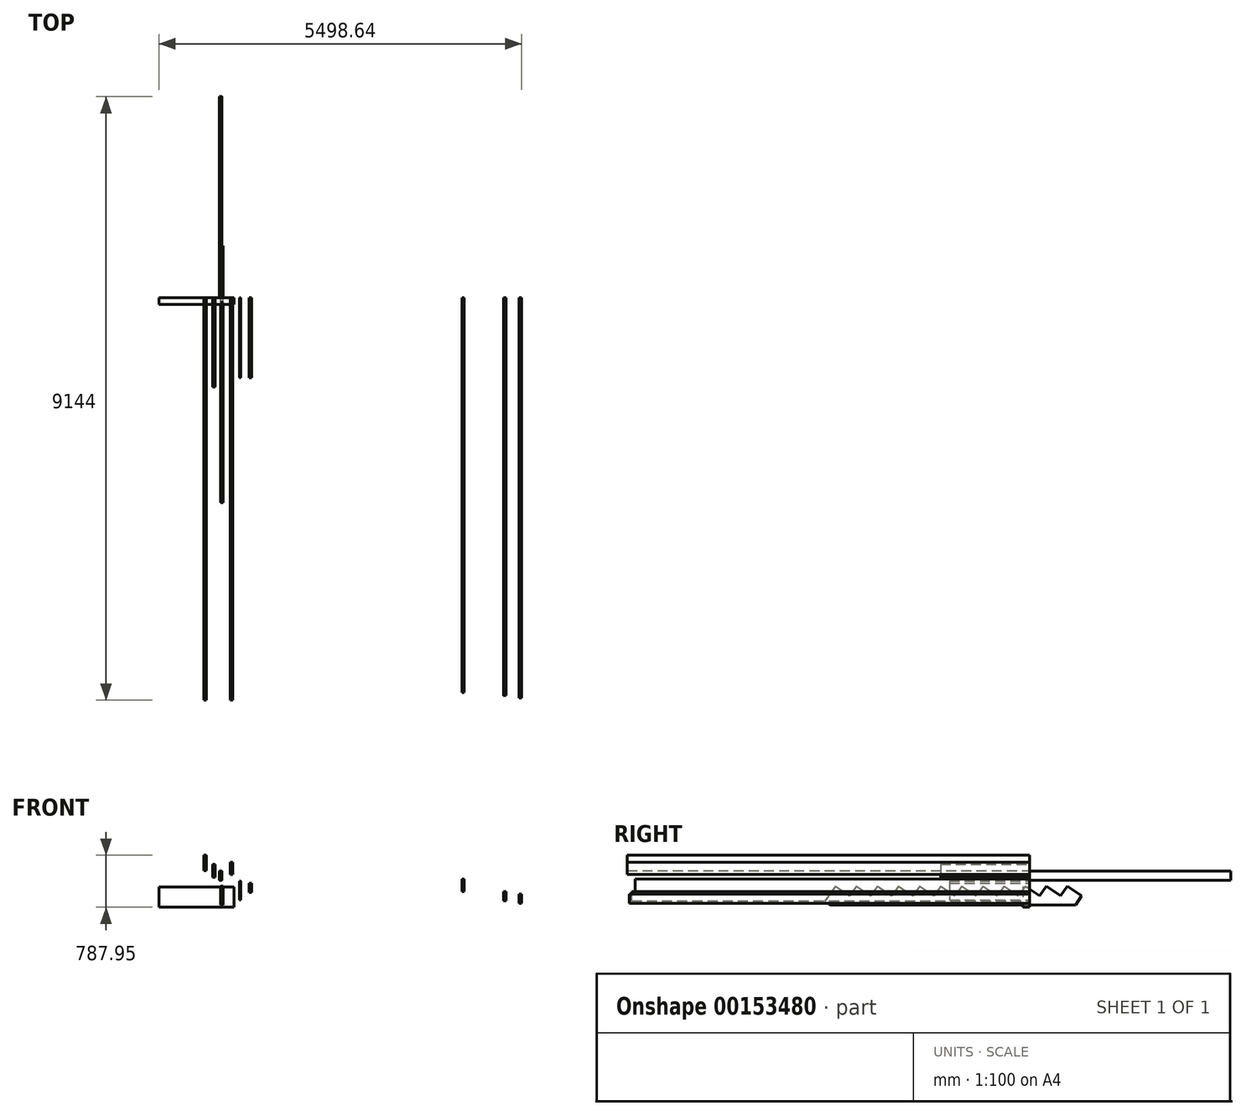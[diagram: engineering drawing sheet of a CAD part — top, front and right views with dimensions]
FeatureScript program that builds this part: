
annotation { "Feature Type Name" : "Feature", "Feature Type Description" : "" }
export const myFeature = defineFeature(function(context is Context, id is Id, definition is map)
    precondition{}
    {
        {
            var Q0;
            Q0=qCreatedBy(makeId("Front.planeOp"),FACE);
            var sketch = newSketch(context, id + "F0", { "sketchPlane" : qUnion([Q0])});
            skLineSegment(sketch, "E0.bottom", {"start": v(-15.87, 69.85) * mm, "end": v(15.88, 69.85) * mm});
            skLineSegment(sketch, "E0.top", {"start": v(-15.88, -69.85) * mm, "end": v(15.87, -69.85) * mm});
            skLineSegment(sketch, "E0.left", {"start": v(-19.05, 66.68) * mm, "end": v(-19.05, -66.68) * mm});
            skLineSegment(sketch, "E0.right", {"start": v(19.05, 66.68) * mm, "end": v(19.05, -66.68) * mm});
            skPoint(sketch, "E0.middle", {"position": v(0, 0) * mm});
            skPoint(sketch, "E1.visualSharp", {"position": v(-19.05, 69.85) * mm});
            skArc(sketch, "E1.filletArc", {"start": v(-15.87, 69.85) * mm, "mid": v(-18.12, 68.92) * mm, "end": v(-19.05, 66.68) * mm});
            skPoint(sketch, "E2.visualSharp", {"position": v(19.05, 69.85) * mm});
            skArc(sketch, "E2.filletArc", {"start": v(19.05, 66.68) * mm, "mid": v(18.12, 68.92) * mm, "end": v(15.88, 69.85) * mm});
            skPoint(sketch, "E3.visualSharp", {"position": v(19.05, -69.85) * mm});
            skArc(sketch, "E3.filletArc", {"start": v(15.87, -69.85) * mm, "mid": v(18.12, -68.92) * mm, "end": v(19.05, -66.68) * mm});
            skPoint(sketch, "E4.visualSharp", {"position": v(-19.05, -69.85) * mm});
            skArc(sketch, "E4.filletArc", {"start": v(-19.05, -66.68) * mm, "mid": v(-18.12, -68.92) * mm, "end": v(-15.88, -69.85) * mm});
            skSolve(sketch);
        }
        {
            var Q0;
            Q0=makeQuery(id+"F0.imprint","IMPRINT",FACE,{"disambiguationData":[TD([[makeQuery(id+"F0.imprint","IMPRINT",EDGE,{"derivedFrom":sQuery(id+"F0.wireOp",EDGE,"E0.bottom")}),-1.0]])]});
            extrude(context, id + "F1", {"entities" : qUnion([Q0]), "oppositeDirection" : true, "depth" : 3048 * mm});
        }
        {
            var Q0;
            Q0=qCreatedBy(makeId("Front.planeOp"),FACE);
            var sketch = newSketch(context, id + "F2", { "sketchPlane" : qUnion([Q0])});
            skLineSegment(sketch, "E5.bottom", {"start": v(183.25, 20.22) * mm, "end": v(145.15, 20.22) * mm});
            skLineSegment(sketch, "E5.top", {"start": v(183.25, 204.37) * mm, "end": v(145.15, 204.37) * mm});
            skLineSegment(sketch, "E5.left", {"start": v(183.25, 20.22) * mm, "end": v(183.25, 204.37) * mm});
            skLineSegment(sketch, "E5.right", {"start": v(145.15, 20.22) * mm, "end": v(145.15, 204.37) * mm});
            skPoint(sketch, "E5.middle", {"position": v(164.2, 112.3) * mm});
            skPoint(sketch, "E6.visualSharp", {"position": v(145.15, 204.37) * mm});
            skLineSegment(sketch, "E6.filletArc", {"start": v(145.15, 204.37) * mm, "end": v(145.15, 204.37) * mm});
            skPoint(sketch, "E7.visualSharp", {"position": v(183.25, 204.37) * mm});
            skLineSegment(sketch, "E7.filletArc", {"start": v(183.25, 204.37) * mm, "end": v(183.25, 204.37) * mm});
            skPoint(sketch, "E8.visualSharp", {"position": v(183.25, 20.22) * mm});
            skLineSegment(sketch, "E8.filletArc", {"start": v(183.25, 20.22) * mm, "end": v(183.25, 20.22) * mm});
            skPoint(sketch, "E9.visualSharp", {"position": v(145.15, 20.22) * mm});
            skLineSegment(sketch, "E9.filletArc", {"start": v(145.15, 20.22) * mm, "end": v(145.15, 20.22) * mm});
            skSolve(sketch);
        }
        {
            var Q0;
            Q0=makeQuery(id+"F2.imprint","IMPRINT",FACE,{"disambiguationData":[TD([[makeQuery(id+"F2.imprint","IMPRINT",EDGE,{"derivedFrom":sQuery(id+"F2.wireOp",EDGE,"E5.bottom")}),-1.0]])]});
            extrude(context, id + "F3", {"entities" : qUnion([Q0]), "depth" : 50.8 * mm});
        }
        {
            var Q0;
            Q0=makeQuery(id+"F3.opExtrude","CAP_FACE",FACE,{"disambiguationData":[OSD([sQuery(id+"F2.wireOp",EDGE,"E5.bottom"),sQuery(id+"F2.wireOp",EDGE,"E5.top"),sQuery(id+"F2.wireOp",EDGE,"E5.left"),sQuery(id+"F2.wireOp",EDGE,"E5.right"),sQuery(id+"F2.wireOp",EDGE,"E6.filletArc"),sQuery(id+"F2.wireOp",EDGE,"E7.filletArc"),sQuery(id+"F2.wireOp",EDGE,"E8.filletArc"),sQuery(id+"F2.wireOp",EDGE,"E9.filletArc")])],"isStart":false});
            extrude(context, id + "F4", {"entities" : qUnion([Q0]), "operationType" : NewBodyOperationType.ADD, "depth" : 6045.2 * mm});
        }
        {
            var Q0;
            Q0=qCreatedBy(makeId("Front.planeOp"),FACE);
            var sketch = newSketch(context, id + "F5", { "sketchPlane" : qUnion([Q0])});
            skLineSegment(sketch, "E10.bottom", {"start": v(-219.82, 74.1) * mm, "end": v(-257.92, 74.1) * mm});
            skLineSegment(sketch, "E10.top", {"start": v(-219.82, 309.04) * mm, "end": v(-257.92, 309.04) * mm});
            skLineSegment(sketch, "E10.left", {"start": v(-219.82, 74.1) * mm, "end": v(-219.82, 309.04) * mm});
            skLineSegment(sketch, "E10.right", {"start": v(-257.92, 74.1) * mm, "end": v(-257.92, 309.04) * mm});
            skPoint(sketch, "E10.middle", {"position": v(-238.87, 191.57) * mm});
            skSolve(sketch);
        }
        {
            var Q0;
            Q0=makeQuery(id+"F5.imprint","IMPRINT",FACE,{"disambiguationData":[TD([[makeQuery(id+"F5.imprint","IMPRINT",EDGE,{"derivedFrom":sQuery(id+"F5.wireOp",EDGE,"E10.bottom")}),-1.0]])]});
            extrude(context, id + "F6", {"entities" : qUnion([Q0]), "depth" : 6096 * mm});
        }
        {
            var Q0;
            Q0=qCreatedBy(makeId("Front.planeOp"),FACE);
            var sketch = newSketch(context, id + "F7", { "sketchPlane" : qUnion([Q0])});
            skLineSegment(sketch, "E11.bottom", {"start": v(193, 138.2) * mm, "end": v(332.7, 138.2) * mm});
            skLineSegment(sketch, "E11.top", {"start": v(193, 119.14) * mm, "end": v(332.7, 119.14) * mm});
            skLineSegment(sketch, "E11.left", {"start": v(193, 138.2) * mm, "end": v(193, 119.14) * mm});
            skLineSegment(sketch, "E11.right", {"start": v(332.7, 138.2) * mm, "end": v(332.7, 119.14) * mm});
            skSolve(sketch);
        }
        {
            var Q0;
            Q0=makeQuery(id+"F7.imprint","IMPRINT",FACE,{"disambiguationData":[TD([[makeQuery(id+"F7.imprint","IMPRINT",EDGE,{"derivedFrom":sQuery(id+"F7.wireOp",EDGE,"E11.bottom")}),-1.0]])]});
            extrude(context, id + "F8", {"entities" : qUnion([Q0]), "depth" : 1137.67 * mm});
        }
        {
            var Q0;
            Q0=makeQuery(id+"F8.opExtrude","CAP_FACE",FACE,{"disambiguationData":[OSD([sQuery(id+"F7.wireOp",EDGE,"E11.bottom"),sQuery(id+"F7.wireOp",EDGE,"E11.top"),sQuery(id+"F7.wireOp",EDGE,"E11.left"),sQuery(id+"F7.wireOp",EDGE,"E11.right")])],"isStart":false});
            var sketch = newSketch(context, id + "F9", { "sketchPlane" : qUnion([Q0])});
            skLineSegment(sketch, "E12.bottom", {"start": v(193, 119.14) * mm, "end": v(186.65, 119.14) * mm});
            skLineSegment(sketch, "E12.top", {"start": v(193, 138.2) * mm, "end": v(186.65, 138.2) * mm});
            skLineSegment(sketch, "E12.left", {"start": v(193, 119.14) * mm, "end": v(193, 138.2) * mm});
            skLineSegment(sketch, "E12.right", {"start": v(186.65, 119.14) * mm, "end": v(186.65, 138.2) * mm});
            skSolve(sketch);
        }
        {
            var Q0;
            Q0=makeQuery(id+"F1.opExtrude","SWEPT_FACE",FACE,{"disambiguationData":[OSD([sQuery(id+"F0.wireOp",EDGE,"E0.top")])]});
            var sketch = newSketch(context, id + "F10", { "sketchPlane" : qUnion([Q0])});
            skPoint(sketch, "E13.endSnap0", {"position": v(0, 0) * mm});
            skPoint(sketch, "E14", {"position": v(0, -38.1) * mm});
            skSolve(sketch);
        }
        {
            var Q0;
            Q0=makeQuery(id+"F9.imprint","IMPRINT",FACE,{"disambiguationData":[TD([[makeQuery(id+"F9.imprint","IMPRINT",EDGE,{"derivedFrom":sQuery(id+"F9.wireOp",EDGE,"E12.left")}),1.0]])]});
            extrude(context, id + "F11", {"entities" : qUnion([Q0]), "operationType" : NewBodyOperationType.ADD, "oppositeDirection" : true, "depth" : 1219.2 * mm});
        }
        {
            var Q0;
            Q0=makeQuery(id+"F8.opExtrude","SWEPT_BODY",BODY,{"disambiguationData":[OSD([sQuery(id+"F7.wireOp",EDGE,"E11.bottom"),sQuery(id+"F7.wireOp",EDGE,"E11.top"),sQuery(id+"F7.wireOp",EDGE,"E11.left"),sQuery(id+"F7.wireOp",EDGE,"E11.right")])]});
            transform(context, id + "F12", {"entities" : qUnion([Q0]), "transformType" : TransformType.TRANSLATION_3D, "dx" : 0 * mm, "dy" : 0 * mm, "dz" : 0 * mm, "makeCopy" : true});
        }
        {
            var Q0;
            Q0=makeQuery(id+"F8.opExtrude","SWEPT_BODY",BODY,{"disambiguationData":[OSD([sQuery(id+"F7.wireOp",EDGE,"E11.bottom"),sQuery(id+"F7.wireOp",EDGE,"E11.top"),sQuery(id+"F7.wireOp",EDGE,"E11.left"),sQuery(id+"F7.wireOp",EDGE,"E11.right")])]});
            transform(context, id + "F13", {"entities" : qUnion([Q0]), "transformType" : TransformType.TRANSLATION_3D, "dx" : 0 * mm, "dy" : 0 * mm, "dz" : 0 * mm, "makeCopy" : true});
        }
        {
            var Q0;
            Q0=makeQuery(id+"F12.opPattern","COPY",BODY,{"derivedFrom":makeQuery(id+"F8.opExtrude","SWEPT_BODY",BODY,{"disambiguationData":[OSD([sQuery(id+"F7.wireOp",EDGE,"E11.bottom"),sQuery(id+"F7.wireOp",EDGE,"E11.top"),sQuery(id+"F7.wireOp",EDGE,"E11.left"),sQuery(id+"F7.wireOp",EDGE,"E11.right")])]}),"instanceName":"1"});
            deleteBodies(context, id + "F14", {"entities" : qUnion([Q0])});
        }
        {
            var Q0;
            Q0=makeQuery(id+"F13.opPattern","COPY",BODY,{"derivedFrom":makeQuery(id+"F8.opExtrude","SWEPT_BODY",BODY,{"disambiguationData":[OSD([sQuery(id+"F7.wireOp",EDGE,"E11.bottom"),sQuery(id+"F7.wireOp",EDGE,"E11.top"),sQuery(id+"F7.wireOp",EDGE,"E11.left"),sQuery(id+"F7.wireOp",EDGE,"E11.right")])]}),"instanceName":"1"});
            deleteBodies(context, id + "F15", {"entities" : qUnion([Q0])});
        }
        {
            var Q0;
            Q0=makeQuery(id+"F8.opExtrude","SWEPT_BODY",BODY,{"disambiguationData":[OSD([sQuery(id+"F7.wireOp",EDGE,"E11.bottom"),sQuery(id+"F7.wireOp",EDGE,"E11.top"),sQuery(id+"F7.wireOp",EDGE,"E11.left"),sQuery(id+"F7.wireOp",EDGE,"E11.right")])]});
            deleteBodies(context, id + "F16", {"entities" : qUnion([Q0])});
        }
        {
            var Q0;
            Q0=qCreatedBy(makeId("Front.planeOp"),FACE);
            var sketch = newSketch(context, id + "F17", { "sketchPlane" : qUnion([Q0])});
            skLineSegment(sketch, "E15.bottom", {"start": v(-120.79, 170.88) * mm, "end": v(-82.69, 170.88) * mm});
            skLineSegment(sketch, "E15.top", {"start": v(-120.79, -25.97) * mm, "end": v(-82.69, -25.97) * mm});
            skLineSegment(sketch, "E15.left", {"start": v(-120.79, 170.88) * mm, "end": v(-120.79, -25.97) * mm});
            skLineSegment(sketch, "E15.right", {"start": v(-82.69, 170.88) * mm, "end": v(-82.69, -25.97) * mm});
            skSolve(sketch);
        }
        {
            var Q0;
            Q0=makeQuery(id+"F17.imprint","IMPRINT",FACE,{"disambiguationData":[TD([[makeQuery(id+"F17.imprint","IMPRINT",EDGE,{"derivedFrom":sQuery(id+"F17.wireOp",EDGE,"E15.bottom")}),-1.0]])]});
            extrude(context, id + "F18", {"entities" : qUnion([Q0]), "depth" : 1349.38 * mm});
        }
        {
            var Q0;
            Q0=qCreatedBy(makeId("Right.planeOp"),FACE);
            var sketch = newSketch(context, id + "F19", { "sketchPlane" : qUnion([Q0])});
            skLineSegment(sketch, "E16.bottom", {"start": v(693.46, -443.05) * mm, "end": v(-3027.46, -443.05) * mm});
            skLineSegment(sketch, "E17", {"start": v(-2626.14, -156.32) * mm, "end": v(-2728.6, -305.5) * mm});
            skLineSegment(sketch, "E18", {"start": v(-2945.83, -156.32) * mm, "end": v(-2728.6, -305.5) * mm});
            skLineSegment(sketch, "E19.1.0.0", {"start": v(-2626.48, -156.8) * mm, "end": v(-2409.25, -306) * mm});
            skLineSegment(sketch, "E19.1.0.1", {"start": v(-2306.8, -156.8) * mm, "end": v(-2409.25, -306) * mm});
            skLineSegment(sketch, "E19.2.0.0", {"start": v(-2306.8, -156.8) * mm, "end": v(-2089.57, -306) * mm});
            skLineSegment(sketch, "E19.2.0.1", {"start": v(-1987.12, -156.8) * mm, "end": v(-2089.57, -306) * mm});
            skLineSegment(sketch, "E19.3.0.0", {"start": v(-1987.12, -156.8) * mm, "end": v(-1769.88, -306) * mm});
            skLineSegment(sketch, "E19.3.0.1", {"start": v(-1667.43, -156.8) * mm, "end": v(-1769.88, -306) * mm});
            skLineSegment(sketch, "E19.4.0.0", {"start": v(-1667.43, -156.8) * mm, "end": v(-1450.2, -306) * mm});
            skLineSegment(sketch, "E19.4.0.1", {"start": v(-1347.75, -156.8) * mm, "end": v(-1450.2, -306) * mm});
            skLineSegment(sketch, "E19.5.0.0", {"start": v(-1347.75, -156.8) * mm, "end": v(-1130.52, -306) * mm});
            skLineSegment(sketch, "E19.5.0.1", {"start": v(-1028.07, -156.8) * mm, "end": v(-1130.52, -306) * mm});
            skLineSegment(sketch, "E19.6.0.0", {"start": v(-1028.07, -156.8) * mm, "end": v(-810.83, -306) * mm});
            skLineSegment(sketch, "E19.6.0.1", {"start": v(-708.38, -156.8) * mm, "end": v(-810.83, -306) * mm});
            skLineSegment(sketch, "E19.7.0.0", {"start": v(-708.38, -156.8) * mm, "end": v(-491.15, -306) * mm});
            skLineSegment(sketch, "E19.7.0.1", {"start": v(-388.7, -156.8) * mm, "end": v(-491.15, -306) * mm});
            skLineSegment(sketch, "E19.8.0.0", {"start": v(-388.7, -156.8) * mm, "end": v(-171.47, -306) * mm});
            skLineSegment(sketch, "E19.8.0.1", {"start": v(-69.02, -156.8) * mm, "end": v(-171.47, -306) * mm});
            skLineSegment(sketch, "E19.9.0.0", {"start": v(-69.02, -156.8) * mm, "end": v(148.21, -306) * mm});
            skLineSegment(sketch, "E19.9.0.1", {"start": v(250.67, -156.8) * mm, "end": v(148.21, -306) * mm});
            skLineSegment(sketch, "E20.1.0.0", {"start": v(250.67, -156.8) * mm, "end": v(467.9, -306) * mm});
            skLineSegment(sketch, "E20.1.0.1", {"start": v(570.35, -156.8) * mm, "end": v(467.9, -306) * mm});
            skLineSegment(sketch, "E20.2.0.0", {"start": v(570.01, -157.3) * mm, "end": v(787.24, -306.49) * mm});
            skLineSegment(sketch, "E20.2.0.1", {"start": v(787.24, -306.49) * mm, "end": v(693.46, -443.05) * mm});
            skLineSegment(sketch, "E21", {"start": v(-2945.83, -156.32) * mm, "end": v(-3105.8, -389.25) * mm});
            skLineSegment(sketch, "E22", {"start": v(-2945.83, -156.32) * mm, "end": v(-3037.5, -289.8) * mm});
            skLineSegment(sketch, "E23", {"start": v(-3037.5, -289.8) * mm, "end": v(-3105.8, -389.25) * mm});
            skLineSegment(sketch, "E24.0", {"start": v(-3105.8, -389.25) * mm, "end": v(-3027.46, -443.05) * mm});
            skSolve(sketch);
        }
        {
            var Q0;
            Q0=makeQuery(id+"F19.imprint","IMPRINT",FACE,{"disambiguationData":[TD([[makeQuery(id+"F19.imprint","IMPRINT",EDGE,{"derivedFrom":sQuery(id+"F19.wireOp",EDGE,"E16.bottom")}),-1.0]])]});
            extrude(context, id + "F20", {"entities" : qUnion([Q0]), "depth" : 38.1 * mm});
        }
        {
            var Q0;
            Q0=qCreatedBy(makeId("Front.planeOp"),FACE);
            var sketch = newSketch(context, id + "F21", { "sketchPlane" : qUnion([Q0])});
            skLineSegment(sketch, "E25.bottom", {"start": v(432.14, -114.4) * mm, "end": v(470.24, -114.4) * mm});
            skLineSegment(sketch, "E25.top", {"start": v(432.14, -254.1) * mm, "end": v(470.24, -254.1) * mm});
            skLineSegment(sketch, "E25.left", {"start": v(432.14, -114.4) * mm, "end": v(432.14, -254.1) * mm});
            skLineSegment(sketch, "E25.right", {"start": v(470.24, -114.4) * mm, "end": v(470.24, -254.1) * mm});
            skSolve(sketch);
        }
        {
            var Q0;
            Q0=makeQuery(id+"F21.imprint","IMPRINT",FACE,{"disambiguationData":[TD([[makeQuery(id+"F21.imprint","IMPRINT",EDGE,{"derivedFrom":sQuery(id+"F21.wireOp",EDGE,"E25.bottom")}),-1.0]])]});
            extrude(context, id + "F22", {"entities" : qUnion([Q0]), "depth" : 1213.87 * mm});
        }
        {
            var Q0;
            Q0=qCreatedBy(makeId("Front.planeOp"),FACE);
            var sketch = newSketch(context, id + "F23", { "sketchPlane" : qUnion([Q0])});
            skLineSegment(sketch, "E26.bottom", {"start": v(282.17, -80.3) * mm, "end": v(298.04, -80.3) * mm});
            skLineSegment(sketch, "E26.top", {"start": v(282.17, -366.05) * mm, "end": v(301.22, -366.05) * mm});
            skLineSegment(sketch, "E26.left", {"start": v(282.17, -80.3) * mm, "end": v(282.17, -366.05) * mm});
            skLineSegment(sketch, "E26.right", {"start": v(301.22, -83.48) * mm, "end": v(301.22, -366.05) * mm});
            skPoint(sketch, "E27.visualSharp", {"position": v(301.22, -80.3) * mm});
            skArc(sketch, "E27.filletArc", {"start": v(301.22, -83.48) * mm, "mid": v(300.29, -81.23) * mm, "end": v(298.04, -80.3) * mm});
            skSolve(sketch);
        }
        {
            var Q0;
            Q0=makeQuery(id+"F23.imprint","IMPRINT",FACE,{"disambiguationData":[TD([[makeQuery(id+"F23.imprint","IMPRINT",EDGE,{"derivedFrom":sQuery(id+"F23.wireOp",EDGE,"E26.bottom")}),-1.0]])]});
            extrude(context, id + "F24", {"entities" : qUnion([Q0]), "depth" : 1213.87 * mm});
        }
        {
            var Q0;
            Q0=makeQuery(id+"F20.opExtrude","CAP_FACE",FACE,{"disambiguationData":[OSD([sQuery(id+"F19.wireOp",EDGE,"E16.bottom"),sQuery(id+"F19.wireOp",EDGE,"E17"),sQuery(id+"F19.wireOp",EDGE,"E18"),sQuery(id+"F19.wireOp",EDGE,"E19.1.0.0"),sQuery(id+"F19.wireOp",EDGE,"E19.1.0.1"),sQuery(id+"F19.wireOp",EDGE,"E19.2.0.0"),sQuery(id+"F19.wireOp",EDGE,"E19.2.0.1"),sQuery(id+"F19.wireOp",EDGE,"E19.3.0.0"),sQuery(id+"F19.wireOp",EDGE,"E19.3.0.1"),sQuery(id+"F19.wireOp",EDGE,"E19.4.0.0"),sQuery(id+"F19.wireOp",EDGE,"E19.4.0.1"),sQuery(id+"F19.wireOp",EDGE,"E19.5.0.0"),sQuery(id+"F19.wireOp",EDGE,"E19.5.0.1"),sQuery(id+"F19.wireOp",EDGE,"E19.6.0.0"),sQuery(id+"F19.wireOp",EDGE,"E19.6.0.1"),sQuery(id+"F19.wireOp",EDGE,"E19.7.0.0"),sQuery(id+"F19.wireOp",EDGE,"E19.7.0.1"),sQuery(id+"F19.wireOp",EDGE,"E19.8.0.0"),sQuery(id+"F19.wireOp",EDGE,"E19.8.0.1"),sQuery(id+"F19.wireOp",EDGE,"E19.9.0.0"),sQuery(id+"F19.wireOp",EDGE,"E19.9.0.1"),sQuery(id+"F19.wireOp",EDGE,"E20.1.0.0"),sQuery(id+"F19.wireOp",EDGE,"E20.1.0.1"),sQuery(id+"F19.wireOp",EDGE,"E20.2.0.0"),sQuery(id+"F19.wireOp",EDGE,"E20.2.0.1"),sQuery(id+"F19.wireOp",EDGE,"E22"),sQuery(id+"F19.wireOp",EDGE,"E23"),sQuery(id+"F19.wireOp",EDGE,"E24.0")])],"isStart":false});
            var sketch = newSketch(context, id + "F25", { "sketchPlane" : qUnion([Q0])});
            skLineSegment(sketch, "E28", {"start": v(-3105.8, -389.25) * mm, "end": v(-3037.08, -289.2) * mm});
            skPoint(sketch, "E29.endSnap0", {"position": v(740.35, -374.77) * mm});
            skLineSegment(sketch, "E30.1.0.0", {"start": v(-1873.86, -389.81) * mm, "end": v(-1873.86, -312.8) * mm});
            skLineSegment(sketch, "E30.2.0.0", {"start": v(-641.54, -389.81) * mm, "end": v(-641.54, -312.8) * mm});
            skPoint(sketch, "E31.orphan", {"position": v(730.62, -389.81) * mm});
            skLineSegment(sketch, "E32", {"start": v(-1873.86, -389.81) * mm, "end": v(-1801.42, -284.33) * mm});
            skLineSegment(sketch, "E33", {"start": v(-641.54, -389.81) * mm, "end": v(-554.23, -262.68) * mm});
            skLineSegment(sketch, "E34", {"start": v(890.24, -157.4) * mm, "end": v(-2945.83, -156.32) * mm});
            skLineSegment(sketch, "E35", {"start": v(730.62, -389.81) * mm, "end": v(890.24, -157.4) * mm});
            skSolve(sketch);
        }
        {
            var Q0;
            Q0=qCreatedBy(makeId("Front.planeOp"),FACE);
            var sketch = newSketch(context, id + "F26", { "sketchPlane" : qUnion([Q0])});
            skLineSegment(sketch, "E36.bottom", {"start": v(-5292.13, 2373.84) * mm, "end": v(-2244.13, 2373.84) * mm});
            skLineSegment(sketch, "E36.top", {"start": v(-5292.13, -2198.16) * mm, "end": v(-2244.13, -2198.16) * mm});
            skLineSegment(sketch, "E36.left", {"start": v(-5292.13, 2373.84) * mm, "end": v(-5292.13, -2198.16) * mm});
            skLineSegment(sketch, "E36.right", {"start": v(-2244.13, 2373.84) * mm, "end": v(-2244.13, -2198.16) * mm});
            skSolve(sketch);
        }
        {
            var Q0;
            Q0 = qSketchRegion(id + "F26", true);
            extrude(context, id + "F27", {"entities" : qUnion([Q0]), "depth" : 152.4 * mm});
        }
        {
            var Q0;
            Q0=makeQuery(id+"F27.opExtrude","SWEPT_BODY",BODY,{"disambiguationData":[OSD([sQuery(id+"F26.wireOp",EDGE,"E36.bottom"),sQuery(id+"F26.wireOp",EDGE,"E36.top"),sQuery(id+"F26.wireOp",EDGE,"E36.left"),sQuery(id+"F26.wireOp",EDGE,"E36.right")])]});
            deleteBodies(context, id + "F28", {"entities" : qUnion([Q0])});
        }
        {
            var Q0;
            Q0=qCreatedBy(makeId("Front.planeOp"),FACE);
            var sketch = newSketch(context, id + "F29", { "sketchPlane" : qUnion([Q0])});
            skLineSegment(sketch, "E37.bottom", {"start": v(3653.07, -48.79) * mm, "end": v(3691.17, -48.79) * mm});
            skLineSegment(sketch, "E37.top", {"start": v(3653.07, -239.29) * mm, "end": v(3691.17, -239.29) * mm});
            skLineSegment(sketch, "E37.left", {"start": v(3653.07, -48.79) * mm, "end": v(3653.07, -239.29) * mm});
            skLineSegment(sketch, "E37.right", {"start": v(3691.17, -48.79) * mm, "end": v(3691.17, -239.29) * mm});
            skSolve(sketch);
        }
        {
            var Q0;
            Q0 = qSketchRegion(id + "F29", true);
            extrude(context, id + "F30", {"entities" : qUnion([Q0]), "depth" : 5980.05 * mm});
        }
        {
            var Q0;
            Q0=qCreatedBy(makeId("Front.planeOp"),FACE);
            var sketch = newSketch(context, id + "F31", { "sketchPlane" : qUnion([Q0])});
            skLineSegment(sketch, "E38.bottom", {"start": v(4324.84, -243.97) * mm, "end": v(4286.74, -243.97) * mm});
            skLineSegment(sketch, "E38.top", {"start": v(4324.84, -383.67) * mm, "end": v(4286.74, -383.67) * mm});
            skLineSegment(sketch, "E38.left", {"start": v(4324.84, -243.97) * mm, "end": v(4324.84, -383.67) * mm});
            skLineSegment(sketch, "E38.right", {"start": v(4286.74, -243.97) * mm, "end": v(4286.74, -383.67) * mm});
            skSolve(sketch);
        }
        {
            var Q0;
            Q0 = qSketchRegion(id + "F31", true);
            extrude(context, id + "F32", {"entities" : qUnion([Q0]), "depth" : 6066.16 * mm});
        }
        {
            var Q0;
            Q0=makeQuery(id+"F32.opExtrude","SWEPT_FACE",FACE,{"disambiguationData":[OSD([sQuery(id+"F31.wireOp",EDGE,"E38.bottom")])]});
            var sketch = newSketch(context, id + "F33", { "sketchPlane" : qUnion([Q0])});
            skLineSegment(sketch, "E39", {"start": v(4324.84, -6028.06) * mm, "end": v(4286.74, -6031.39) * mm});
            skLineSegment(sketch, "E40", {"start": v(4286.74, -6031.39) * mm, "end": v(4286.74, -6066.16) * mm});
            skLineSegment(sketch, "E41", {"start": v(4286.74, -6066.16) * mm, "end": v(4324.84, -6066.16) * mm});
            skLineSegment(sketch, "E42", {"start": v(4324.84, -6066.16) * mm, "end": v(4324.84, -6028.06) * mm});
            skLineSegment(sketch, "E43", {"start": v(4324.84, -6028.06) * mm, "end": v(4324.84, -6066.16) * mm});
            skLineSegment(sketch, "E44", {"start": v(4286.74, -6066.16) * mm, "end": v(4286.74, -6031.39) * mm});
            skSolve(sketch);
        }
        {
            var Q0;
            Q0 = qSketchRegion(id + "F33", true);
            extrude(context, id + "F34", {"entities" : qUnion([Q0]), "operationType" : NewBodyOperationType.REMOVE, "oppositeDirection" : true, "depth" : 152.4 * mm});
        }
        {
            var Q0;
            Q0=qCreatedBy(makeId("Front.planeOp"),FACE);
            var sketch = newSketch(context, id + "F35", { "sketchPlane" : qUnion([Q0])});
            skLineSegment(sketch, "E45.bottom", {"start": v(4522.62, -282.63) * mm, "end": v(4560.72, -282.63) * mm});
            skLineSegment(sketch, "E45.top", {"start": v(4522.62, -422.33) * mm, "end": v(4560.72, -422.33) * mm});
            skLineSegment(sketch, "E45.left", {"start": v(4522.62, -282.63) * mm, "end": v(4522.62, -422.33) * mm});
            skLineSegment(sketch, "E45.right", {"start": v(4560.72, -282.63) * mm, "end": v(4560.72, -422.33) * mm});
            skSolve(sketch);
        }
        {
            var Q0;
            Q0 = qSketchRegion(id + "F35", true);
            extrude(context, id + "F36", {"entities" : qUnion([Q0]), "depth" : 6111.88 * mm});
        }
        {
            var Q0;
            Q0=makeQuery(id+"F36.opExtrude","SWEPT_FACE",FACE,{"disambiguationData":[OSD([sQuery(id+"F35.wireOp",EDGE,"E45.bottom")])]});
            var sketch = newSketch(context, id + "F37", { "sketchPlane" : qUnion([Q0])});
            skLineSegment(sketch, "E46", {"start": v(4560.72, -6061.08) * mm, "end": v(4522.62, -6064.41) * mm});
            skLineSegment(sketch, "E47", {"start": v(4522.62, -6064.41) * mm, "end": v(4522.62, -6111.88) * mm});
            skLineSegment(sketch, "E48", {"start": v(4522.62, -6111.88) * mm, "end": v(4560.72, -6111.88) * mm});
            skLineSegment(sketch, "E49", {"start": v(4560.72, -6111.88) * mm, "end": v(4560.72, -6061.08) * mm});
            skSolve(sketch);
        }
        {
            var Q0;
            Q0 = qSketchRegion(id + "F37", true);
            extrude(context, id + "F38", {"entities" : qUnion([Q0]), "operationType" : NewBodyOperationType.REMOVE, "oppositeDirection" : true, "depth" : 152.4 * mm});
        }
        {
            var Q0;
            Q0=qCreatedBy(makeId("Front.planeOp"),FACE);
            var sketch = newSketch(context, id + "F39", { "sketchPlane" : qUnion([Q0])});
            skLineSegment(sketch, "E50.bottom", {"start": v(-937.92, -174.11) * mm, "end": v(199.75, -174.11) * mm});
            skLineSegment(sketch, "E50.top", {"start": v(-937.92, -478.91) * mm, "end": v(199.75, -478.91) * mm});
            skLineSegment(sketch, "E50.left", {"start": v(-937.92, -174.11) * mm, "end": v(-937.92, -478.91) * mm});
            skLineSegment(sketch, "E50.right", {"start": v(199.75, -174.11) * mm, "end": v(199.75, -478.91) * mm});
            skSolve(sketch);
        }
        {
            var Q0;
            Q0 = qSketchRegion(id + "F39", true);
            extrude(context, id + "F40", {"entities" : qUnion([Q0]), "depth" : 101.6 * mm});
        }
    });
